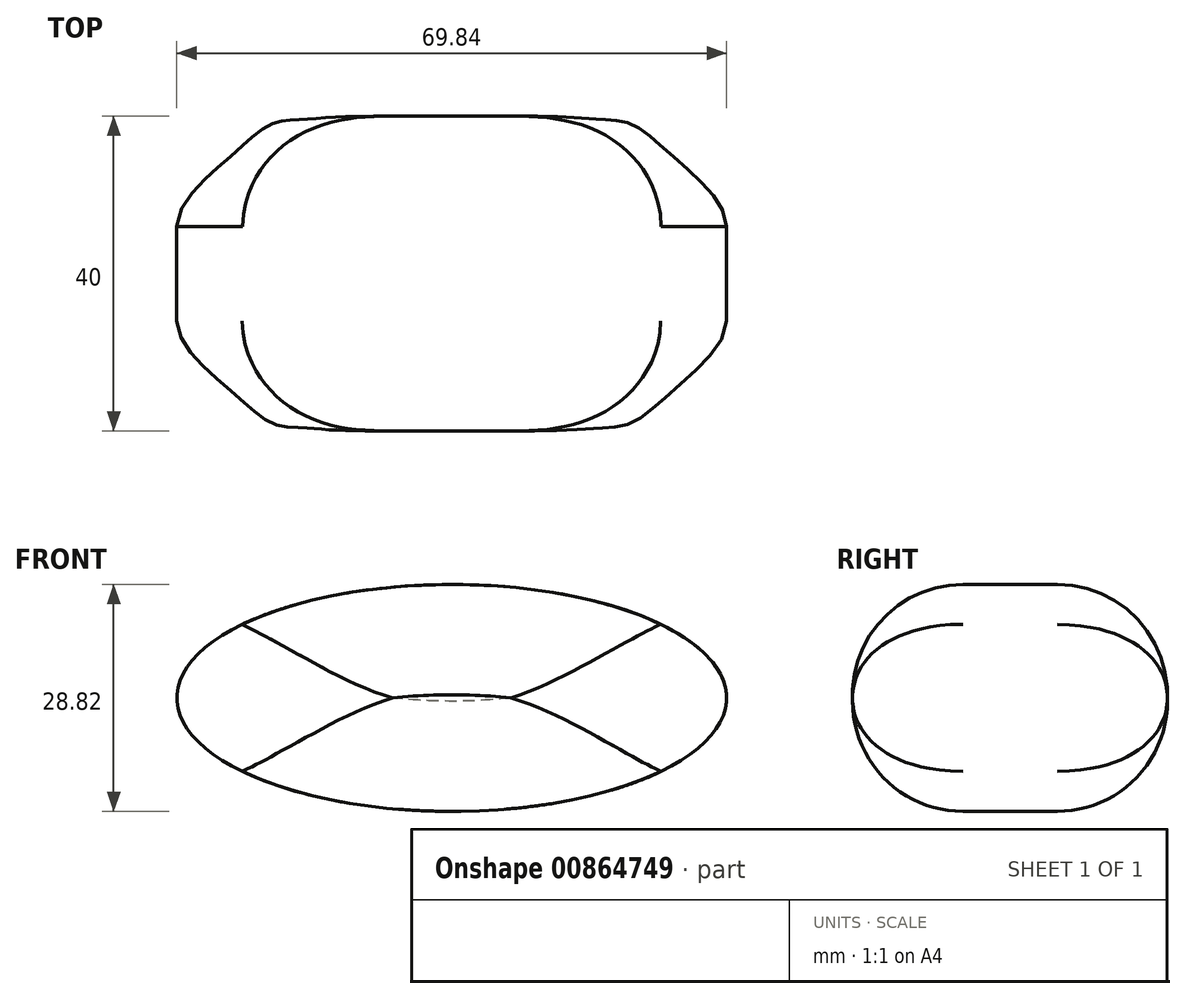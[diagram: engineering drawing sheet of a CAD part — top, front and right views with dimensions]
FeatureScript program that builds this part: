
annotation { "Feature Type Name" : "Feature", "Feature Type Description" : "" }
export const myFeature = defineFeature(function(context is Context, id is Id, definition is map)
    precondition{}
    {
        {
            var Q0;
            Q0=qCreatedBy(makeId("Front.planeOp"),FACE);
            var sketch = newSketch(context, id + "F0", { "sketchPlane" : qUnion([Q0])});
            skEllipse(sketch, "E0", {"center": v(0, 0) * mm, "majorRadius": 34.92 * mm, "minorRadius": 14.4 * mm, "majorAxis": v(1, 0)});
            skSolve(sketch);
        }
        {
            var Q0;
            Q0=makeQuery(id+"F0.imprint","IMPRINT",FACE,{"disambiguationData":[TD([[makeQuery(id+"F0.imprint","IMPRINT",EDGE,{"derivedFrom":sQuery(id+"F0.wireOp",EDGE,"E0")}),1.0]])]});
            extrude(context, id + "F1", {"entities" : qUnion([Q0]), "depth" : 40 * mm, "offsetDistance" : 25 * mm});
        }
        {
            var Q0;
            Q0=makeQuery(id+"F1.opExtrude","CAP_EDGE",EDGE,{"disambiguationData":[OSD([sQuery(id+"F0.wireOp",EDGE,"E0")])],"isStart":false});
            var Q1;
            Q1=makeQuery(id+"F1.opExtrude","CAP_FACE",FACE,{"disambiguationData":[OSD([sQuery(id+"F0.wireOp",EDGE,"E0")])],"isStart":true});
            fillet(context, id + "F2", {"entities" : qUnion([Q0, Q1]), "radius" : 14 * mm, "tangentPropagation" : true, "allowEdgeOverflow" : false});
        }
    });
